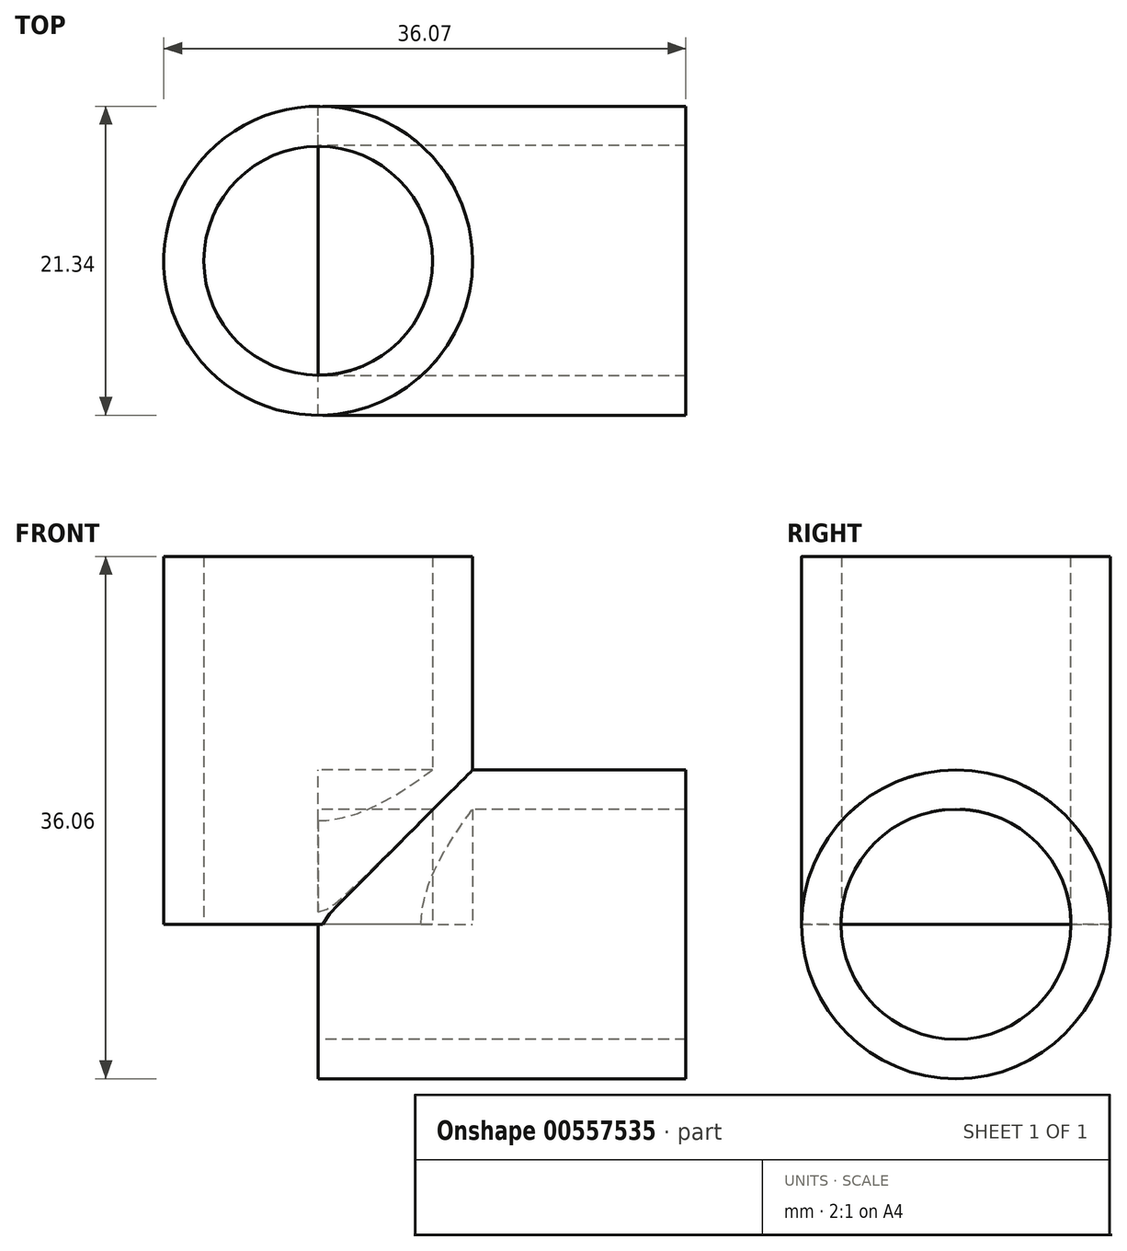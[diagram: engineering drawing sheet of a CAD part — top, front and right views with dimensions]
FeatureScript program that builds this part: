
annotation { "Feature Type Name" : "Feature", "Feature Type Description" : "" }
export const myFeature = defineFeature(function(context is Context, id is Id, definition is map)
    precondition{}
    {
        {
            var Q0;
            Q0=qCreatedBy(makeId("Top.planeOp"),FACE);
            var sketch = newSketch(context, id + "F0", { "sketchPlane" : qUnion([Q0])});
            skCircle(sketch, "E0", {"center": v(0, 0) * mm, "radius": 10.67 * mm});
            skCircle(sketch, "E1", {"center": v(0, 0) * mm, "radius": 7.9 * mm});
            skSolve(sketch);
        }
        {
            var Q0;
            Q0=makeQuery(id+"F0.imprint","IMPRINT",FACE,{"disambiguationData":[TD([[makeQuery(id+"F0.imprint","IMPRINT",EDGE,{"derivedFrom":sQuery(id+"F0.wireOp",EDGE,"E0")}),1.0]])]});
            extrude(context, id + "F1", {"entities" : qUnion([Q0]), "depth" : 25.4 * mm, "offsetDistance" : 25.4 * mm});
        }
        {
            var Q0;
            Q0=qCreatedBy(makeId("Right.planeOp"),FACE);
            var sketch = newSketch(context, id + "F2", { "sketchPlane" : qUnion([Q0])});
            skCircle(sketch, "E2", {"center": v(0, 0) * mm, "radius": 10.66 * mm});
            skCircle(sketch, "E3", {"center": v(0, 0) * mm, "radius": 7.94 * mm});
            skSolve(sketch);
        }
        {
            var Q0;
            Q0=makeQuery(id+"F2.imprint","IMPRINT",FACE,{"disambiguationData":[TD([[makeQuery(id+"F2.imprint","IMPRINT",EDGE,{"derivedFrom":sQuery(id+"F2.wireOp",EDGE,"E2")}),1.0]])]});
            extrude(context, id + "F3", {"entities" : qUnion([Q0]), "operationType" : NewBodyOperationType.ADD, "depth" : 25.4 * mm, "offsetDistance" : 25.4 * mm});
        }
    });
